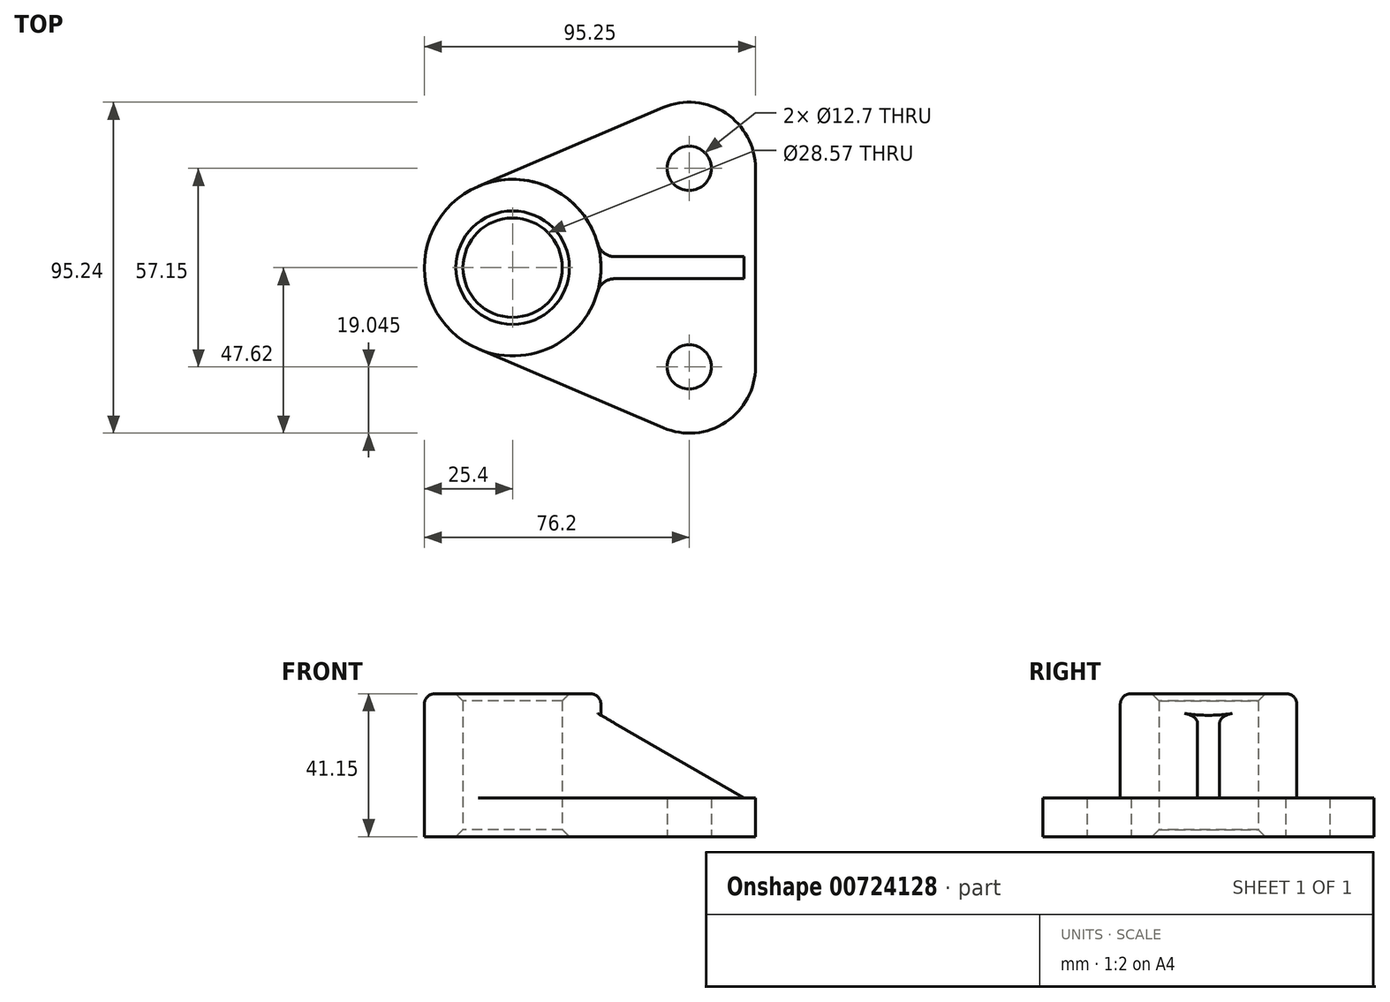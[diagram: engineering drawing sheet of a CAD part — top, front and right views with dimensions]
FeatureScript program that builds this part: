
annotation { "Feature Type Name" : "Feature", "Feature Type Description" : "" }
export const myFeature = defineFeature(function(context is Context, id is Id, definition is map)
    precondition{}
    {
        {
            var Q0;
            Q0=qCreatedBy(makeId("Top.planeOp"),FACE);
            var sketch = newSketch(context, id + "F0", { "sketchPlane" : qUnion([Q0])});
            skCircle(sketch, "E0", {"center": v(0, 0) * mm, "radius": 14.29 * mm});
            skCircle(sketch, "E1", {"center": v(0, 0) * mm, "radius": 25.4 * mm});
            skLineSegment(sketch, "E2", {"start": v(0, 0) * mm, "end": v(50.8, 0) * mm});
            skLineSegment(sketch, "E3", {"start": v(50.8, 0) * mm, "end": v(50.8, -28.58) * mm});
            skCircle(sketch, "E4", {"center": v(50.8, -28.58) * mm, "radius": 6.35 * mm});
            skLineSegment(sketch, "E5", {"start": v(50.8, 0) * mm, "end": v(50.8, 28.58) * mm});
            skCircle(sketch, "E6", {"center": v(50.8, 28.58) * mm, "radius": 6.35 * mm});
            skCircle(sketch, "E7", {"center": v(50.8, 28.58) * mm, "radius": 19.05 * mm});
            skCircle(sketch, "E8", {"center": v(50.8, -28.58) * mm, "radius": 19.05 * mm});
            skLineSegment(sketch, "E9", {"start": v(43.33, 46.1) * mm, "end": v(-9.97, 23.36) * mm});
            skLineSegment(sketch, "E10", {"start": v(69.85, 28.58) * mm, "end": v(69.85, -28.58) * mm});
            skLineSegment(sketch, "E11", {"start": v(43.33, -46.1) * mm, "end": v(-9.97, -23.36) * mm});
            skSolve(sketch);
        }
        {
            var Q0;
            Q0=makeQuery(id+"F0.imprint","IMPRINT",FACE,{"disambiguationData":[TD([[makeQuery(id+"F0.imprint","IMPRINT",EDGE,{"derivedFrom":sQuery(id+"F0.wireOp",EDGE,"E0")}),-1.0]])]});
            extrude(context, id + "F1", {"entities" : qUnion([Q0]), "depth" : 41.15 * mm, "offsetDistance" : 25.4 * mm});
        }
        {
            var Q0;
            {var subQ0=sQuery(id+"F0.wireOp",EDGE,"E9");Q0=makeQuery(id+"F0.imprint","IMPRINT",FACE,{"disambiguationData":[TD([[makeQuery(id+"F0.imprint","IMPRINT",EDGE,{"derivedFrom":subQ0}),1.0]])]});}
            var Q1;
            Q1=makeQuery(id+"F0.imprint","IMPRINT",FACE,{"disambiguationData":[TD([[makeQuery(id+"F0.imprint","IMPRINT",EDGE,{"derivedFrom":sQuery(id+"F0.wireOp",EDGE,"E6")}),-1.0]])]});
            var Q2;
            Q2=makeQuery(id+"F0.imprint","IMPRINT",FACE,{"disambiguationData":[TD([[makeQuery(id+"F0.imprint","IMPRINT",EDGE,{"derivedFrom":sQuery(id+"F0.wireOp",EDGE,"E4")}),-1.0]])]});
            var Q3;
            {var subQ0=sQuery(id+"F0.wireOp",EDGE,"E10");Q3=makeQuery(id+"F0.imprint","IMPRINT",FACE,{"disambiguationData":[TD([[makeQuery(id+"F0.imprint","IMPRINT",EDGE,{"derivedFrom":subQ0}),-1.0]])]});}
            var Q4;
            {var subQ7=sQuery(id+"F0.wireOp",EDGE,"E11");Q4=makeQuery(id+"F0.imprint","IMPRINT",FACE,{"disambiguationData":[TD([[makeQuery(id+"F0.imprint","IMPRINT",EDGE,{"derivedFrom":subQ7}),-1.0]])]});}
            extrude(context, id + "F2", {"entities" : qUnion([Q0, Q1, Q2, Q3, Q4]), "operationType" : NewBodyOperationType.ADD, "depth" : 11.18 * mm, "offsetDistance" : 25.4 * mm});
        }
        {
            var Q0;
            Q0=makeQuery(id+"F1.opExtrude","CAP_EDGE",EDGE,{"disambiguationData":[OSD([sQuery(id+"F0.wireOp",EDGE,"E1")])],"isStart":false});
            fillet(context, id + "F3", {"entities" : qUnion([Q0]), "radius" : 3.05 * mm, "tangentPropagation" : true, "allowEdgeOverflow" : false});
        }
        {
            var Q0;
            Q0=makeQuery(id+"F1.opExtrude","CAP_EDGE",EDGE,{"disambiguationData":[OSD([sQuery(id+"F0.wireOp",EDGE,"E0")])],"isStart":false});
            var Q1;
            Q1=makeQuery(id+"F1.opExtrude","CAP_EDGE",EDGE,{"disambiguationData":[OSD([sQuery(id+"F0.wireOp",EDGE,"E0")])],"isStart":true});
            chamfer(context, id + "F4", {"entities" : qUnion([Q0, Q1]), "chamferType" : ChamferType.OFFSET_ANGLE, "width" : 2.03 * mm, "oppositeDirection" : false, "angle" : 45 * degree, "tangentPropagation" : true});
        }
        {
            var Q0;
            Q0=qCreatedBy(makeId("Front.planeOp"),FACE);
            var sketch = newSketch(context, id + "F5", { "sketchPlane" : qUnion([Q0])});
            skLineSegment(sketch, "E12", {"start": v(23.08, 36.27) * mm, "end": v(66.55, 11.18) * mm});
            skLineSegment(sketch, "E13", {"start": v(66.55, 11.18) * mm, "end": v(22.73, 11.18) * mm});
            skLineSegment(sketch, "E14", {"start": v(22.73, 11.18) * mm, "end": v(23.08, 36.27) * mm});
            skSolve(sketch);
        }
        {
            var Q0;
            Q0=makeQuery(id+"F5.imprint","IMPRINT",FACE,{"disambiguationData":[TD([[makeQuery(id+"F5.imprint","IMPRINT",EDGE,{"derivedFrom":sQuery(id+"F5.wireOp",EDGE,"E12")}),-1.0]])]});
            extrude(context, id + "F6", {"entities" : qUnion([Q0]), "operationType" : NewBodyOperationType.ADD, "depth" : 3.17 * mm, "offsetDistance" : 25.4 * mm});
        }
        {
            var Q0;
            Q0=makeQuery(id+"F5.imprint","IMPRINT",FACE,{"disambiguationData":[TD([[makeQuery(id+"F5.imprint","IMPRINT",EDGE,{"derivedFrom":sQuery(id+"F5.wireOp",EDGE,"E12")}),-1.0]])]});
            extrude(context, id + "F7", {"entities" : qUnion([Q0]), "operationType" : NewBodyOperationType.ADD, "oppositeDirection" : true, "depth" : 3.17 * mm, "offsetDistance" : 25.4 * mm});
        }
        {
            var Q0;
            {var subQ0=sQuery(id+"F0.wireOp",EDGE,"E1");var subQ1=sQuery(id+"F0.wireOp",EDGE,"E11");Q0=makeQuery(id+"F6.boolean.opBoolean","SPLIT",EDGE,{"disambiguationData":[TD([makeQuery(id+"F2.opExtrude","SWEPT_FACE",FACE,{"disambiguationData":[OSD([subQ1])]})])],"derivedFrom":makeQuery(id+"F2.opExtrude","CAP_EDGE",EDGE,{"disambiguationData":[OSD([subQ0])],"isStart":false})});}
            var Q1;
            Q1=makeQuery(id+"F6.opExtrude","CAP_EDGE",EDGE,{"disambiguationData":[OSD([sQuery(id+"F5.wireOp",EDGE,"E13")])],"isStart":false});
            var Q2;
            Q2=makeQuery(id+"F7.opExtrude","CAP_EDGE",EDGE,{"disambiguationData":[OSD([sQuery(id+"F5.wireOp",EDGE,"E13")])],"isStart":false});
            var Q3;
            {var subQ0=sQuery(id+"F0.wireOp",EDGE,"E1");var subQ1=sQuery(id+"F0.wireOp",EDGE,"E9");Q3=makeQuery(id+"F6.boolean.opBoolean","SPLIT",EDGE,{"disambiguationData":[TD([makeQuery(id+"F2.opExtrude","SWEPT_FACE",FACE,{"disambiguationData":[OSD([subQ1])]})])],"derivedFrom":makeQuery(id+"F2.opExtrude","CAP_EDGE",EDGE,{"disambiguationData":[OSD([subQ0])],"isStart":false})});}
            var Q4;
            Q4=makeQuery(id+"F7.boolean.opBoolean","INTERSECT",EDGE,{"derivedFrom":[makeQuery(id+"F1.opExtrude","SWEPT_FACE",FACE,{"disambiguationData":[OSD([sQuery(id+"F0.wireOp",EDGE,"E1")])]}),makeQuery(id+"F7.opExtrude","CAP_FACE",FACE,{"disambiguationData":[OSD([sQuery(id+"F5.wireOp",EDGE,"E12"),sQuery(id+"F5.wireOp",EDGE,"E13"),sQuery(id+"F5.wireOp",EDGE,"E14")])],"isStart":false})]});
            var Q5;
            Q5=makeQuery(id+"F6.boolean.opBoolean","INTERSECT",EDGE,{"derivedFrom":[makeQuery(id+"F1.opExtrude","SWEPT_FACE",FACE,{"disambiguationData":[OSD([sQuery(id+"F0.wireOp",EDGE,"E1")])]}),makeQuery(id+"F6.opExtrude","CAP_FACE",FACE,{"disambiguationData":[OSD([sQuery(id+"F5.wireOp",EDGE,"E12"),sQuery(id+"F5.wireOp",EDGE,"E13"),sQuery(id+"F5.wireOp",EDGE,"E14")])],"isStart":false})]});
            fillet(context, id + "F8", {"entities" : qUnion([Q0, Q1, Q2, Q3, Q4, Q5]), "radius" : 5.08 * mm, "tangentPropagation" : true, "allowEdgeOverflow" : false});
        }
    });
